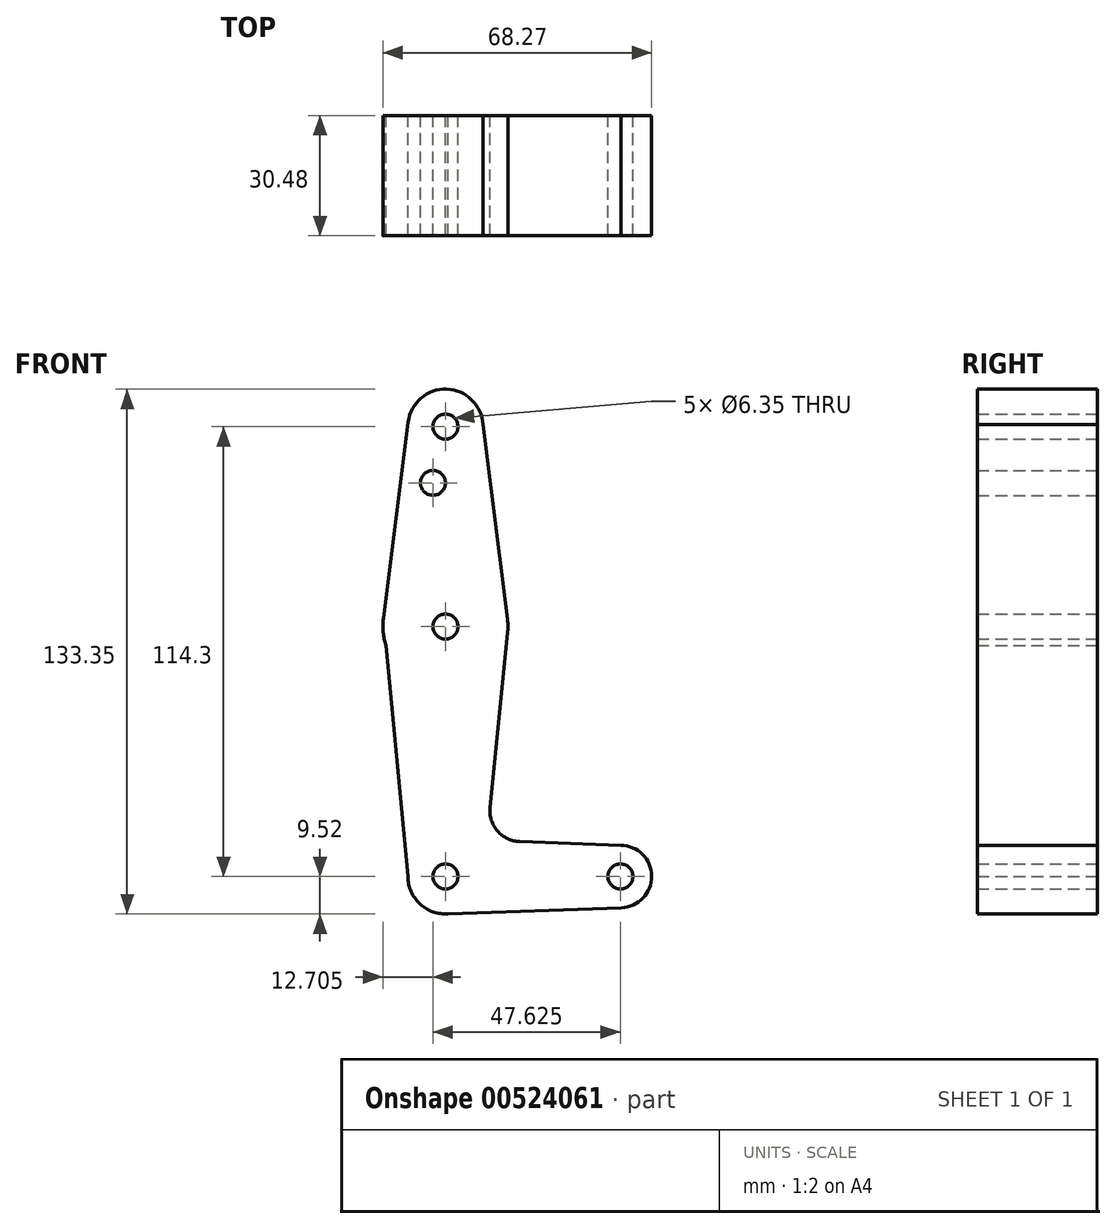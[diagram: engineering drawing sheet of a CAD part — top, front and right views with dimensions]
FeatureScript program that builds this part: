
annotation { "Feature Type Name" : "Feature", "Feature Type Description" : "" }
export const myFeature = defineFeature(function(context is Context, id is Id, definition is map)
    precondition{}
    {
        {
            var Q0;
            Q0=qCreatedBy(makeId("Front.planeOp"),FACE);
            var sketch = newSketch(context, id + "F0", { "sketchPlane" : qUnion([Q0])});
            skCircle(sketch, "E0", {"center": v(0, 114.3) * mm, "radius": 9.53 * mm});
            skCircle(sketch, "E1", {"center": v(44.45, 0) * mm, "radius": 7.94 * mm});
            skCircle(sketch, "E2", {"center": v(0, 63.5) * mm, "radius": 15.88 * mm});
            skCircle(sketch, "E3", {"center": v(0, 0) * mm, "radius": 9.53 * mm});
            skLineSegment(sketch, "E4", {"start": v(9.34, 116.15) * mm, "end": v(15.75, 65.5) * mm});
            skLineSegment(sketch, "E5", {"start": v(11.3, 17.6) * mm, "end": v(15.8, 61.9) * mm});
            skLineSegment(sketch, "E6", {"start": v(-15.76, 65.37) * mm, "end": v(-9.45, 115.5) * mm});
            skLineSegment(sketch, "E7", {"start": v(0, -9.52) * mm, "end": v(44.73, -7.93) * mm});
            skLineSegment(sketch, "E8", {"start": v(44.54, 7.94) * mm, "end": v(18.93, 8.85) * mm});
            skLineSegment(sketch, "E9", {"start": v(-9.52, 0) * mm, "end": v(-15.76, 65.37) * mm});
            skCircle(sketch, "E10", {"center": v(0, 114.3) * mm, "radius": 3.18 * mm});
            skCircle(sketch, "E11", {"center": v(-3.17, 100.03) * mm, "radius": 3.18 * mm});
            skCircle(sketch, "E12", {"center": v(0, 63.5) * mm, "radius": 3.18 * mm});
            skCircle(sketch, "E13", {"center": v(44.45, 0) * mm, "radius": 3.18 * mm});
            skCircle(sketch, "E14", {"center": v(0, 0) * mm, "radius": 3.18 * mm});
            skPoint(sketch, "E15.newPointA", {"position": v(9.52, 0) * mm});
            skPoint(sketch, "E15.newPointB", {"position": v(0, 9.53) * mm});
            skArc(sketch, "E15.filletArc", {"start": v(11.3, 17.6) * mm, "mid": v(13.22, 11.57) * mm, "end": v(18.93, 8.85) * mm});
            skSolve(sketch);
        }
        {
            var Q0;
            Q0 = qSketchRegion(id + "F0", true);
            extrude(context, id + "F1", {"entities" : qUnion([Q0]), "depth" : 30.48 * mm, "offsetDistance" : 25.4 * mm});
        }
    });
